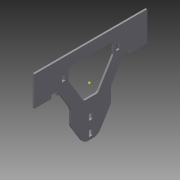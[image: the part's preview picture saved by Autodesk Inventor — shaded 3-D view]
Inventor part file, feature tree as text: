
AUTODESK INVENTOR PART (.ipt)
format: ipt  version: 2015 (Build 190159000, 159)  size: 217,088 bytes
history: native  units: mm
features: extrude x2, fillet x2, sketch x1
ambient origin geometry x8: Origin, YZ Plane, XZ Plane, XY Plane, X Axis, Y Axis, Z Axis, Center Point
bodies: Body1 (feature_tree)
feature tree (5):
  extrude  "Extrusion11"  Depth=200.0mm
  extrude  "Extrusion13"  Depth=10.0mm
  fillet  "Fillet1"  Radius=6.0mm
  fillet  "Fillet2"  Radius=10.0mm
  sketch  "Sketch4"  dims[d8=0.0mm d65=200.0mm d69=20.0mm d71=20.0mm d72=43.5mm d73=43.5mm d74=60.0mm d75=60.0mm d76=10.0mm d77=10.0mm d78=60.0mm d79=90.0mm d80=43.5mm d81=43.5mm d87=15.0mm d115=10.0mm d116=6.0mm d118=10.0mm d119=6.0mm d120=15.0mm d147=65.0mm d173=25.0mm d187=100.0mm d191=30.0mm d192=30.0mm d194=6.000296mm d195=6.0mm d196=10.0mm d197=10.0mm d198=52.999704mm d199=53.0mm d204=150.0mm d210=3.0mm d211=0.0mm d213=20.0mm d214=20.0mm d218=65.0mm d219=40.0mm d220=5.0mm d233=25.922561mm d235=5.0mm d236=20.0mm d237=6.0mm d238=27.0mm d239=10.0mm d240=5.0mm d241=6.0mm d242=10.0mm d243=5.0mm d244=27.0mm d245=10.0mm d246=0.0mm d247=15.0mm d248=5.0mm]
